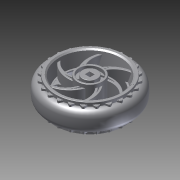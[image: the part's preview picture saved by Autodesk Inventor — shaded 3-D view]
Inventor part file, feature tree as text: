
AUTODESK INVENTOR PART (.ipt)
format: ipt  version: 2013 (Build 170138000, 138)  size: 2,095,616 bytes
history: native  units: mm (DEFAULTED — no unit token found)
features: imported_body x1, sketch x1, other x1, extrude x1
ambient origin geometry x8: Origin, YZ Plane, XZ Plane, XY Plane, X Axis, Y Axis, Z Axis, Center Point
bodies: Solid1 (feature_tree)
feature tree (4):
  imported_body  "Base1"
  sketch  "Sketch1"  dims[d0=25.4mm d1=0.0mm d2=0.0mm d3=0.0mm]
  other  "Srf1"
  extrude  "ExtrusionSrf1"  TaperAngle=0.0deg  [1 undecoded]
note: 1 required parameter value undecoded (feature->parameter linkage not recoverable at this tier; creation-order binding heuristic only, values carry confidence <= 0.55)
